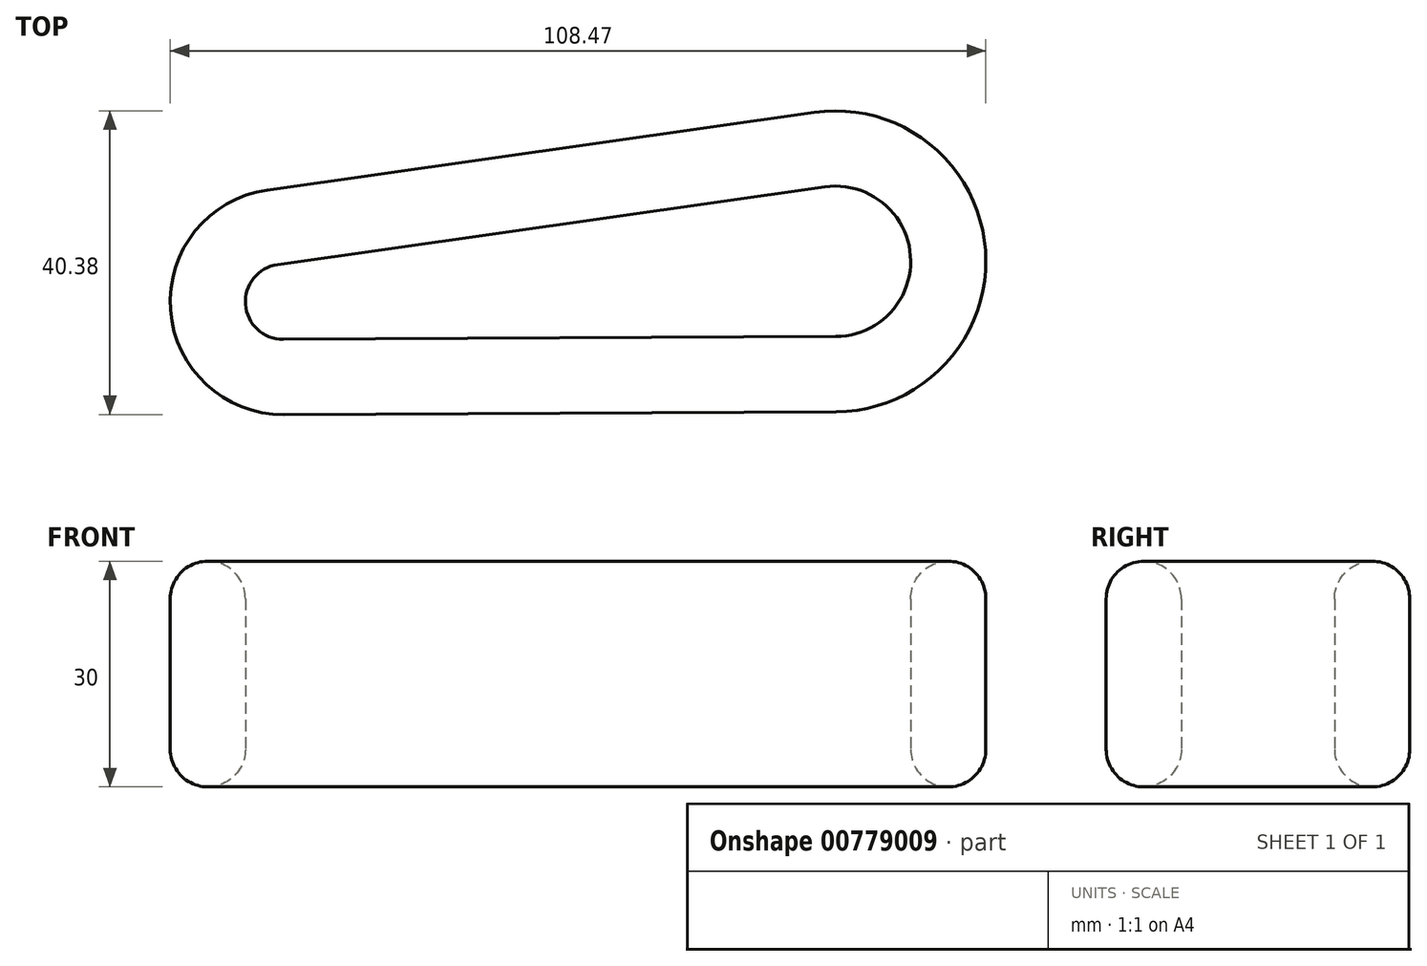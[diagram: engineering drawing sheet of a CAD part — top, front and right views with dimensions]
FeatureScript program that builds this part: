
annotation { "Feature Type Name" : "Feature", "Feature Type Description" : "" }
export const myFeature = defineFeature(function(context is Context, id is Id, definition is map)
    precondition{}
    {
        {
            var Q0;
            Q0=qCreatedBy(makeId("Top.planeOp"),FACE);
            var sketch = newSketch(context, id + "F0", { "sketchPlane" : qUnion([Q0])});
            skArc(sketch, "E0", {"start": v(-38.06, 59.33) * mm, "mid": v(-50.91, 43.38) * mm, "end": v(-35.88, 29.48) * mm});
            skArc(sketch, "E1", {"start": v(37.62, 29.86) * mm, "mid": v(57.47, 51.32) * mm, "end": v(34.71, 69.66) * mm});
            skLineSegment(sketch, "E2", {"start": v(-38.06, 59.33) * mm, "end": v(34.71, 69.66) * mm});
            skLineSegment(sketch, "E3", {"start": v(-35.88, 29.48) * mm, "end": v(37.62, 29.86) * mm});
            skArc(sketch, "E4.0", {"start": v(37.57, 39.86) * mm, "mid": v(47.5, 50.59) * mm, "end": v(36.12, 59.76) * mm});
            skLineSegment(sketch, "E4.1", {"start": v(-36.66, 49.43) * mm, "end": v(36.12, 59.76) * mm});
            skLineSegment(sketch, "E5.0", {"start": v(-35.93, 39.48) * mm, "end": v(37.57, 39.86) * mm});
            skArc(sketch, "E5.1", {"start": v(-36.66, 49.43) * mm, "mid": v(-40.94, 44.11) * mm, "end": v(-35.93, 39.48) * mm});
            skSolve(sketch);
        }
        {
            var Q0;
            Q0 = qSketchRegion(id + "F0", true);
            extrude(context, id + "F1", {"entities" : qUnion([Q0]), "depth" : 30 * mm, "offsetDistance" : 25.4 * mm});
        }
        {
            var Q0;
            Q0 = qSketchRegion(id + "F0", true);
            extrude(context, id + "F2", {"entities" : qUnion([Q0]), "operationType" : NewBodyOperationType.ADD, "depth" : 25.4 * mm, "offsetDistance" : 25.4 * mm});
        }
        {
            var Q0;
            Q0=makeQuery(id+"F1.opExtrude","CAP_FACE",FACE,{"disambiguationData":[OSD([sQuery(id+"F0.wireOp",EDGE,"E0"),sQuery(id+"F0.wireOp",EDGE,"E1"),sQuery(id+"F0.wireOp",EDGE,"E2"),sQuery(id+"F0.wireOp",EDGE,"E3"),sQuery(id+"F0.wireOp",EDGE,"E4.0"),sQuery(id+"F0.wireOp",EDGE,"E4.1"),sQuery(id+"F0.wireOp",EDGE,"E5.0"),sQuery(id+"F0.wireOp",EDGE,"E5.1")])],"isStart":false});
            var Q1;
            Q1=makeQuery(id+"F1.opExtrude","CAP_FACE",FACE,{"disambiguationData":[OSD([sQuery(id+"F0.wireOp",EDGE,"E0"),sQuery(id+"F0.wireOp",EDGE,"E1"),sQuery(id+"F0.wireOp",EDGE,"E2"),sQuery(id+"F0.wireOp",EDGE,"E3"),sQuery(id+"F0.wireOp",EDGE,"E4.0"),sQuery(id+"F0.wireOp",EDGE,"E4.1"),sQuery(id+"F0.wireOp",EDGE,"E5.0"),sQuery(id+"F0.wireOp",EDGE,"E5.1")])],"isStart":true});
            fillet(context, id + "F3", {"entities" : qUnion([Q0, Q1]), "radius" : 5 * mm, "tangentPropagation" : true, "allowEdgeOverflow" : false});
        }
    });
